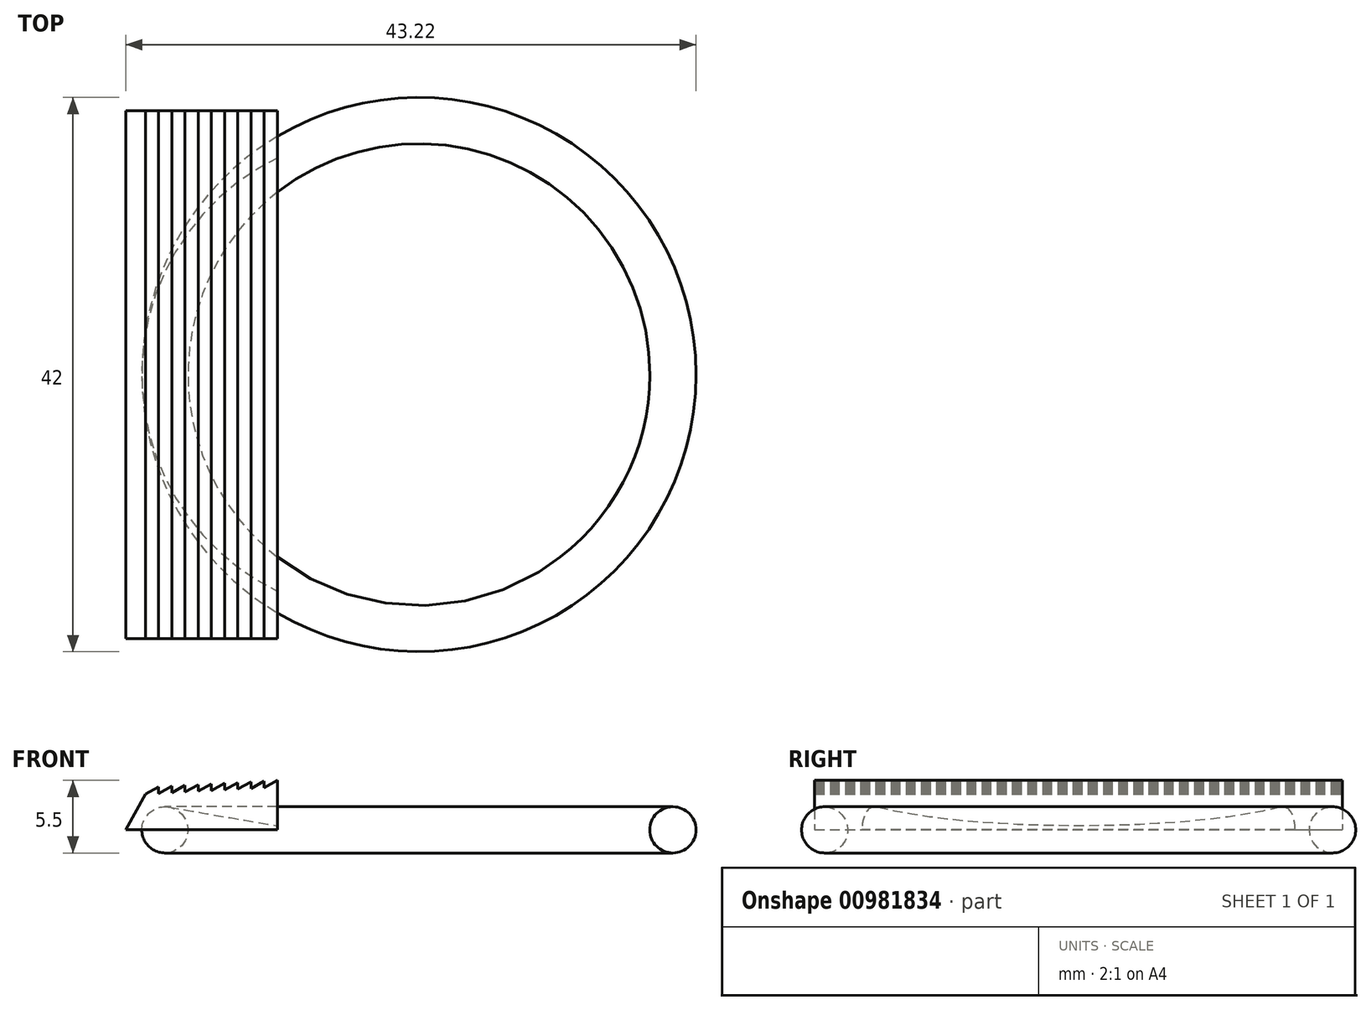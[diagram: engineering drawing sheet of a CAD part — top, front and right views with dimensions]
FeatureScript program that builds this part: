
annotation { "Feature Type Name" : "Feature", "Feature Type Description" : "" }
export const myFeature = defineFeature(function(context is Context, id is Id, definition is map)
    precondition{}
    {
        {
            var Q0;
            Q0=qCreatedBy(makeId("Front.planeOp"),FACE);
            var sketch = newSketch(context, id + "F0", { "sketchPlane" : qUnion([Q0])});
            skLineSegment(sketch, "E0", {"start": v(-22.22, 0) * mm, "end": v(-22.22, 0) * mm});
            skLineSegment(sketch, "E1", {"start": v(-15.72, 3.48) * mm, "end": v(-15.72, 2.98) * mm});
            skLineSegment(sketch, "E2", {"start": v(-15.72, 2.98) * mm, "end": v(-14.72, 3.53) * mm});
            skLineSegment(sketch, "E3", {"start": v(-14.72, 3.53) * mm, "end": v(-14.72, 3.03) * mm});
            skLineSegment(sketch, "E4", {"start": v(-10.72, 3.25) * mm, "end": v(-10.72, 0) * mm});
            skLineSegment(sketch, "E5", {"start": v(-29.04, 2.75) * mm, "end": v(-10.72, 3.75) * mm, "construction": true});
            skLineSegment(sketch, "E6", {"start": v(-29.04, 2.25) * mm, "end": v(-10.72, 3.25) * mm, "construction": true});
            skLineSegment(sketch, "E7", {"start": v(-14.72, 3.03) * mm, "end": v(-13.72, 3.59) * mm});
            skLineSegment(sketch, "E8", {"start": v(-13.72, 3.59) * mm, "end": v(-13.72, 3.09) * mm});
            skLineSegment(sketch, "E9", {"start": v(-13.72, 3.09) * mm, "end": v(-12.72, 3.64) * mm});
            skLineSegment(sketch, "E10", {"start": v(-12.72, 3.64) * mm, "end": v(-12.72, 3.14) * mm});
            skLineSegment(sketch, "E11", {"start": v(-12.72, 3.14) * mm, "end": v(-11.72, 3.7) * mm});
            skLineSegment(sketch, "E12", {"start": v(-11.72, 3.7) * mm, "end": v(-11.72, 3.2) * mm});
            skLineSegment(sketch, "E13", {"start": v(-11.72, 3.2) * mm, "end": v(-10.72, 3.75) * mm});
            skLineSegment(sketch, "E14", {"start": v(-10.72, 3.25) * mm, "end": v(-10.72, 3.75) * mm});
            skLineSegment(sketch, "E15", {"start": v(-15.72, 3.48) * mm, "end": v(-16.72, 2.92) * mm});
            skLineSegment(sketch, "E16", {"start": v(-16.72, 2.92) * mm, "end": v(-16.72, 3.42) * mm});
            skLineSegment(sketch, "E17", {"start": v(-16.72, 3.42) * mm, "end": v(-17.72, 2.87) * mm});
            skLineSegment(sketch, "E18", {"start": v(-17.72, 2.87) * mm, "end": v(-17.72, 3.37) * mm});
            skLineSegment(sketch, "E19", {"start": v(-17.72, 3.37) * mm, "end": v(-18.72, 2.81) * mm});
            skLineSegment(sketch, "E20", {"start": v(-18.72, 2.81) * mm, "end": v(-18.72, 3.31) * mm});
            skLineSegment(sketch, "E21", {"start": v(-18.72, 3.31) * mm, "end": v(-19.72, 2.76) * mm});
            skLineSegment(sketch, "E22", {"start": v(-19.72, 2.76) * mm, "end": v(-19.72, 3.26) * mm});
            skLineSegment(sketch, "E23", {"start": v(-19.72, 3.26) * mm, "end": v(-20.72, 2.7) * mm});
            skLineSegment(sketch, "E24", {"start": v(-20.72, 2.7) * mm, "end": v(-22.22, 0) * mm});
            skLineSegment(sketch, "E25", {"start": v(-22.22, 0) * mm, "end": v(-10.72, 0) * mm});
            skSolve(sketch);
        }
        {
            var Q0;
            Q0=makeQuery(id+"F0.imprint","IMPRINT",FACE,{"disambiguationData":[TD([[makeQuery(id+"F0.imprint","IMPRINT",EDGE,{"derivedFrom":sQuery(id+"F0.wireOp",EDGE,"E1")}),-1.0]])]});
            extrude(context, id + "F1", {"entities" : qUnion([Q0]), "endBound" : BoundingType.SYMMETRIC, "depth" : 40 * mm, "offsetDistance" : 25 * mm});
        }
        {
            var Q0;
            Q0=qCreatedBy(makeId("Top.planeOp"),FACE);
            var sketch = newSketch(context, id + "F2", { "sketchPlane" : qUnion([Q0])});
            skCircle(sketch, "E26", {"center": v(0, 0) * mm, "radius": 18.25 * mm});
            skArc(sketch, "E27", {"start": v(0, 18.25) * mm, "mid": v(-18.25, 0) * mm, "end": v(0, -18.25) * mm});
            skSolve(sketch);
        }
        {
            var Q0;
            Q0=qCreatedBy(makeId("Front.planeOp"),FACE);
            var sketch = newSketch(context, id + "F3", { "sketchPlane" : qUnion([Q0])});
            skCircle(sketch, "E28", {"center": v(-19.25, 0) * mm, "radius": 1.75 * mm});
            skLineSegment(sketch, "E29", {"start": v(0, 0) * mm, "end": v(-10.25, 0) * mm, "construction": true});
            skLineSegment(sketch, "E30", {"start": v(-10.25, 0) * mm, "end": v(-10.25, 0.22) * mm});
            skLineSegment(sketch, "E31", {"start": v(-10.25, 0.22) * mm, "end": v(-18.95, 1.72) * mm});
            skLineSegment(sketch, "E32", {"start": v(-19.25, 0) * mm, "end": v(-10.25, 0) * mm, "construction": true});
            skLineSegment(sketch, "E33.MirrorCS", {"start": v(-10.25, -0.22) * mm, "end": v(-18.95, -1.72) * mm});
            skLineSegment(sketch, "E34.MirrorCS", {"start": v(-10.25, 0) * mm, "end": v(-10.25, -0.22) * mm});
            skSolve(sketch);
        }
        {
            var Q0;
            Q0=makeQuery(id+"F3.imprint","IMPRINT",FACE,{"disambiguationData":[TD([[makeQuery(id+"F3.imprint","IMPRINT",EDGE,{"derivedFrom":sQuery(id+"F3.wireOp",EDGE,"E28")}),1.0]])]});
            var Q1;
            Q1=sQuery(id+"F2.wireOp",EDGE,"E26");
            sweep(context, id + "F4", {"profiles" : qUnion([Q0]), "path" : qUnion([Q1])});
        }
        {
            var Q0;
            Q0=qCreatedBy(makeId("Top.planeOp"),FACE);
            var sketch = newSketch(context, id + "F5", { "sketchPlane" : qUnion([Q0])});
            skArc(sketch, "E35", {"start": v(0, 18.25) * mm, "mid": v(-18.25, 0) * mm, "end": v(0, -18.25) * mm});
            skSolve(sketch);
        }
        {
            var Q0;
            Q0 = qSketchRegion(id + "F3", true);
            var Q1;
            Q1 = qConstructionFilter(qBodyType(qCreatedBy(id + "F5" ,EDGE), BodyType.WIRE), ConstructionObject.NO);
            sweep(context, id + "F6", {"profiles" : qUnion([Q0]), "path" : qUnion([Q1]), "keepProfileOrientation" : true});
        }
        {
            var Q0;
            Q0=makeQuery(id+"F6.opSweep","SWEPT_BODY",BODY,{"disambiguationData":[OSD([sQuery(id+"F3.wireOp",EDGE,"E28"),sQuery(id+"F3.wireOp",EDGE,"E30"),sQuery(id+"F3.wireOp",EDGE,"E31"),sQuery(id+"F3.wireOp",EDGE,"E33.MirrorCS"),sQuery(id+"F3.wireOp",EDGE,"E34.MirrorCS"),sQuery(id+"F5.wireOp",EDGE,"E35")])]});
            var Q1;
            Q1=makeQuery(id+"F1.opExtrude","SWEPT_BODY",BODY,{"disambiguationData":[OSD([sQuery(id+"F0.wireOp",EDGE,"E1"),sQuery(id+"F0.wireOp",EDGE,"E2"),sQuery(id+"F0.wireOp",EDGE,"E3"),sQuery(id+"F0.wireOp",EDGE,"E4"),sQuery(id+"F0.wireOp",EDGE,"E7"),sQuery(id+"F0.wireOp",EDGE,"E8"),sQuery(id+"F0.wireOp",EDGE,"E9"),sQuery(id+"F0.wireOp",EDGE,"E10"),sQuery(id+"F0.wireOp",EDGE,"E11"),sQuery(id+"F0.wireOp",EDGE,"E12"),sQuery(id+"F0.wireOp",EDGE,"E13"),sQuery(id+"F0.wireOp",EDGE,"E14"),sQuery(id+"F0.wireOp",EDGE,"E15"),sQuery(id+"F0.wireOp",EDGE,"E16"),sQuery(id+"F0.wireOp",EDGE,"E17"),sQuery(id+"F0.wireOp",EDGE,"E18"),sQuery(id+"F0.wireOp",EDGE,"E19"),sQuery(id+"F0.wireOp",EDGE,"E20"),sQuery(id+"F0.wireOp",EDGE,"E21"),sQuery(id+"F0.wireOp",EDGE,"E22"),sQuery(id+"F0.wireOp",EDGE,"E23"),sQuery(id+"F0.wireOp",EDGE,"E24"),sQuery(id+"F0.wireOp",EDGE,"E25")])]});
            booleanBodies(context, id + "F7", {"operationType" : BooleanOperationType.SUBTRACTION, "tools" : qUnion([Q0]), "targets" : qUnion([Q1])});
        }
    });
